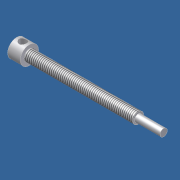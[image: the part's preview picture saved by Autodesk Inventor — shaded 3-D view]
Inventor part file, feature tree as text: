
AUTODESK INVENTOR PART (.ipt)
format: ipt  version: unknown  size: 180,736 bytes
history: native  units: in
note: dims shown in document units (in); Inventor stores cm internally (conversion verified against a paired STEP export)
features: sketch x2, revolve x1, thread x1, plane x1, hole x1
ambient origin geometry x8: Origin, YZ Plane, XZ Plane, XY Plane, X Axis, Y Axis, Z Axis, Center Point
bodies: Solid1 (feature_tree)
feature tree (6):
  revolve  "Revolution1"  [1 undecoded]
  thread  "Thread1"  [1 undecoded]
  plane  "Work Plane1"
  hole  "Hole1"  [1 undecoded]
  sketch  "Sketch1"  dims[d0=0.3125in d1=0.1875in d2=0.125in]
  sketch  "Sketch2"  dims[d3=0.4375in d4=4.1875in d5=5.0625in d6=90.0deg d7=1.0in d8=0.0in d9=0.266in d10=0.75in d11=0.375in d12=0.25in d13=0.5635in d14=1.0in d15=0.8108in]
note: 3 required parameter values undecoded (feature->parameter linkage not recoverable at this tier; creation-order binding heuristic only, values carry confidence <= 0.55)